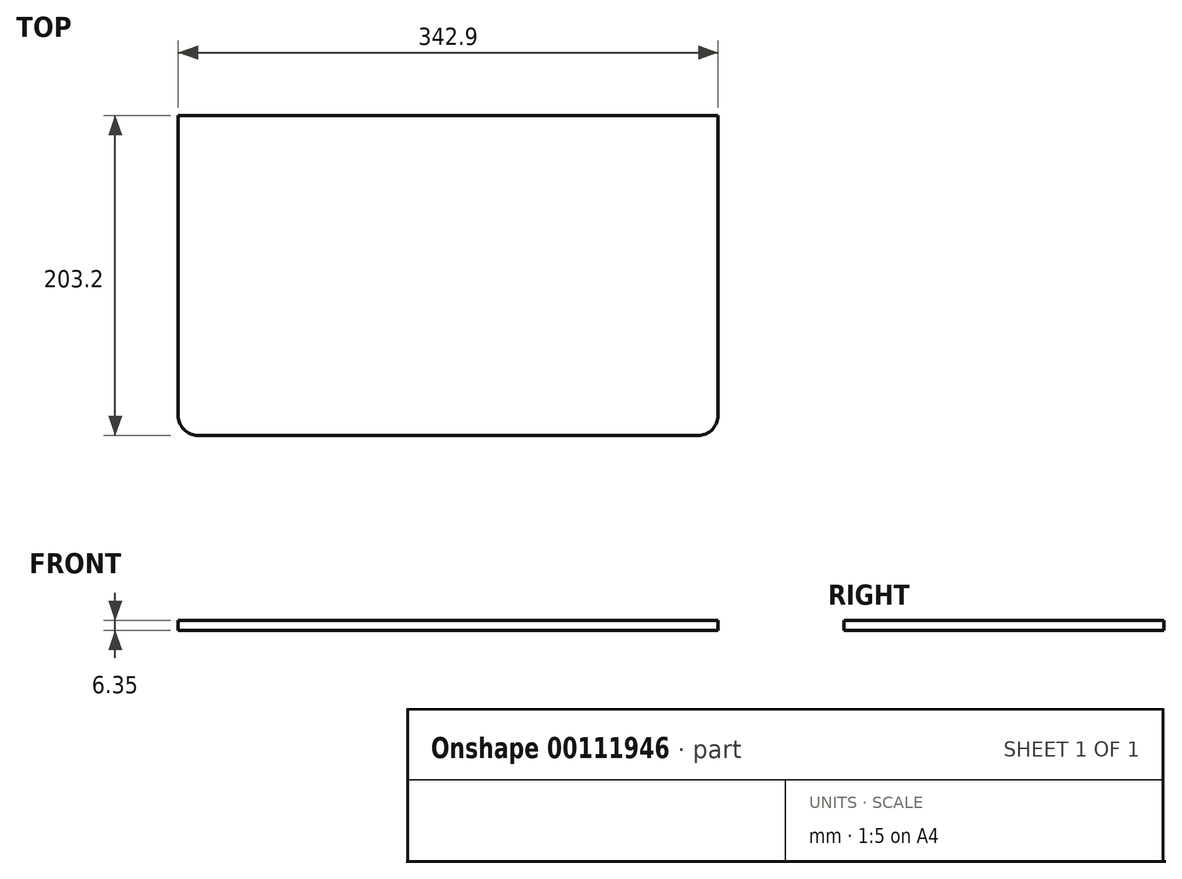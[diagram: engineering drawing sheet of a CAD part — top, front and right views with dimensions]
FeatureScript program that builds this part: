
annotation { "Feature Type Name" : "Feature", "Feature Type Description" : "" }
export const myFeature = defineFeature(function(context is Context, id is Id, definition is map)
    precondition{}
    {
        {
            var Q0;
            Q0=qCreatedBy(makeId("Top.planeOp"),FACE);
            var sketch = newSketch(context, id + "F0", { "sketchPlane" : qUnion([Q0])});
            skLineSegment(sketch, "E0.bottom", {"start": v(-171.45, 101.6) * mm, "end": v(171.45, 101.6) * mm});
            skLineSegment(sketch, "E0.top", {"start": v(-171.45, -101.6) * mm, "end": v(171.45, -101.6) * mm});
            skLineSegment(sketch, "E0.left", {"start": v(-171.45, 101.6) * mm, "end": v(-171.45, -101.6) * mm});
            skLineSegment(sketch, "E0.right", {"start": v(171.45, 101.6) * mm, "end": v(171.45, -101.6) * mm});
            skPoint(sketch, "E0.middle", {"position": v(0, 0) * mm});
            skSolve(sketch);
        }
        {
            var Q0;
            Q0=makeQuery(id+"F0.imprint","IMPRINT",FACE,{"disambiguationData":[TD([[makeQuery(id+"F0.imprint","IMPRINT",EDGE,{"derivedFrom":sQuery(id+"F0.wireOp",EDGE,"E0.bottom")}),-1.0]])]});
            extrude(context, id + "F1", {"entities" : qUnion([Q0]), "depth" : 6.35 * mm});
        }
        {
            var Q0;
            Q0=makeQuery(id+"F1.opExtrude","SWEPT_EDGE",EDGE,{"disambiguationData":[OSD([sQuery(id+"F0.wireOp",EDGE,"E0.top"),sQuery(id+"F0.wireOp",EDGE,"E0.left")])]});
            var Q1;
            Q1=makeQuery(id+"F1.opExtrude","SWEPT_EDGE",EDGE,{"disambiguationData":[OSD([sQuery(id+"F0.wireOp",EDGE,"E0.top"),sQuery(id+"F0.wireOp",EDGE,"E0.right")])]});
            fillet(context, id + "F2", {"entities" : qUnion([Q0, Q1]), "radius" : 12.7 * mm, "tangentPropagation" : true, "allowEdgeOverflow" : false});
        }
    });
